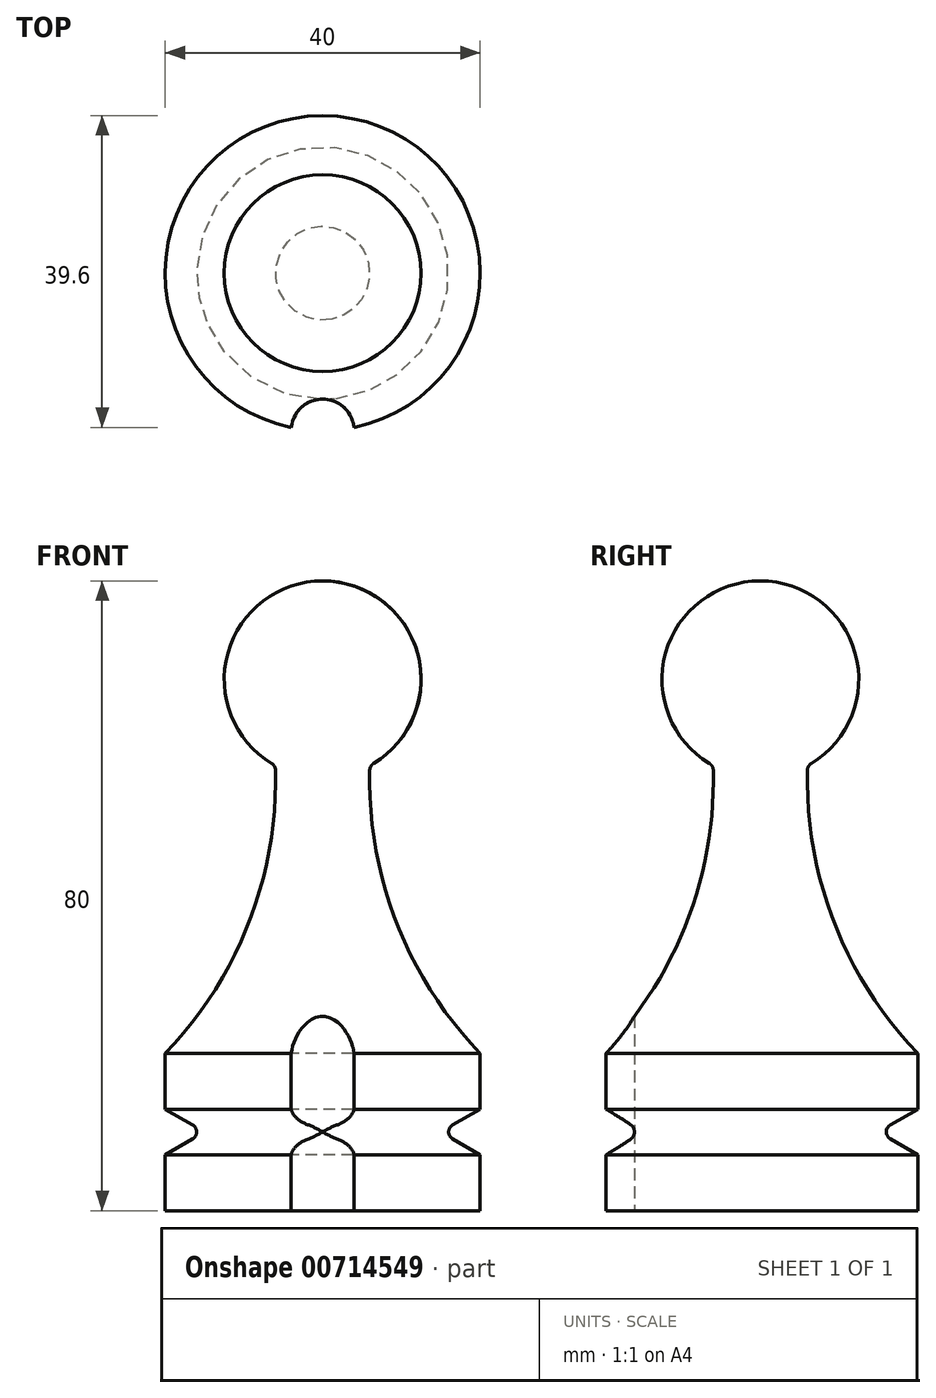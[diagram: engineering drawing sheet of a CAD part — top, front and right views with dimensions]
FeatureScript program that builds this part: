
annotation { "Feature Type Name" : "Feature", "Feature Type Description" : "" }
export const myFeature = defineFeature(function(context is Context, id is Id, definition is map)
    precondition{}
    {
        {
            var Q0;
            Q0=qCreatedBy(makeId("Front.planeOp"),FACE);
            var sketch = newSketch(context, id + "F0", { "sketchPlane" : qUnion([Q0])});
            skLineSegment(sketch, "E0", {"start": v(0, 100) * mm, "end": v(0, -61.55) * mm, "construction": true});
            skLineSegment(sketch, "E1", {"start": v(0, 0) * mm, "end": v(20, 0) * mm, "construction": true});
            skLineSegment(sketch, "E2", {"start": v(20, 0) * mm, "end": v(20, 7.11) * mm, "construction": true});
            skLineSegment(sketch, "E3", {"start": v(15, 10) * mm, "end": v(20, 7.11) * mm, "construction": true});
            skLineSegment(sketch, "E4", {"start": v(20, 12.89) * mm, "end": v(15, 10) * mm});
            skLineSegment(sketch, "E5", {"start": v(20, 12.89) * mm, "end": v(20, 20) * mm});
            skArc(sketch, "E6", {"start": v(6, 56.53) * mm, "mid": v(9.28, 36.84) * mm, "end": v(20, 20) * mm});
            skArc(sketch, "E7", {"start": v(6, 56.53) * mm, "mid": v(12.11, 70.6) * mm, "end": v(0, 80) * mm});
            skLineSegment(sketch, "E8", {"start": v(0, 80) * mm, "end": v(0, 0) * mm});
            skLineSegment(sketch, "E9", {"start": v(15, 10) * mm, "end": v(20, 7.11) * mm});
            skLineSegment(sketch, "E10", {"start": v(20, 7.11) * mm, "end": v(20, 0) * mm});
            skLineSegment(sketch, "E11", {"start": v(0, 0) * mm, "end": v(20, 0) * mm});
            skSolve(sketch);
        }
        {
            var Q0;
            Q0=makeQuery(id+"F0.imprint","IMPRINT",FACE,{"disambiguationData":[TD([[makeQuery(id+"F0.imprint","IMPRINT",EDGE,{"derivedFrom":sQuery(id+"F0.wireOp",EDGE,"E4")}),-1.0]])]});
            var Q1;
            Q1=sQuery(id+"F0.wireOp",EDGE,"E0");
            revolve(context, id + "F1", {"surfaceOperationType" : NewSurfaceOperationType.NEW, "entities" : qUnion([Q0]), "axis" : qUnion([Q1]), "revolveType" : RevolveType.FULL});
        }
        {
            var Q0;
            Q0=makeQuery(id+"F1.opRevolve","SWEPT_FACE",FACE,{"disambiguationData":[OSD([sQuery(id+"F0.wireOp",EDGE,"E11")])]});
            var sketch = newSketch(context, id + "F2", { "sketchPlane" : qUnion([Q0])});
            skCircle(sketch, "E12", {"center": v(0, 20) * mm, "radius": 4 * mm});
            skSolve(sketch);
        }
        {
            var Q0;
            {var subQ0=sQuery(id+"F2.wireOp",EDGE,"E12");var subQ1=makeQuery(id+"F1.opRevolve","SWEPT_EDGE",EDGE,{"disambiguationData":[OSD([sQuery(id+"F0.wireOp",EDGE,"E10"),sQuery(id+"F0.wireOp",EDGE,"E11")])]});var subQ2=makeQuery(id+"F2.imprint","INTERSECT",VERTEX,{"disambiguationData":[OD(0.0)],"derivedFrom":[subQ1,subQ0]});Q0=makeQuery(id+"F2.imprint","IMPRINT",FACE,{"disambiguationData":[TD([[makeQuery(id+"F2.imprint","IMPRINT",EDGE,{"disambiguationData":[TD([[subQ2,-1.0]])],"derivedFrom":subQ0}),1.0]])]});}
            extrude(context, id + "F3", {"entities" : qUnion([Q0]), "operationType" : NewBodyOperationType.REMOVE, "oppositeDirection" : true, "depth" : 34.3 * mm, "offsetDistance" : 25 * mm});
        }
        {
            var Q0;
            Q0=makeQuery(id+"F1.opRevolve","SWEPT_EDGE",EDGE,{"disambiguationData":[OSD([sQuery(id+"F0.wireOp",EDGE,"E4"),sQuery(id+"F0.wireOp",EDGE,"E9")])]});
            fillet(context, id + "F4", {"entities" : qUnion([Q0]), "radius" : 1 * mm, "tangentPropagation" : true, "allowEdgeOverflow" : false});
        }
        {
            var Q0;
            Q0=makeQuery(id+"F1.opRevolve","SWEPT_EDGE",EDGE,{"disambiguationData":[OSD([sQuery(id+"F0.wireOp",EDGE,"E6"),sQuery(id+"F0.wireOp",EDGE,"E7")])]});
            fillet(context, id + "F5", {"entities" : qUnion([Q0]), "radius" : 1 * mm, "tangentPropagation" : true, "allowEdgeOverflow" : false});
        }
    });
